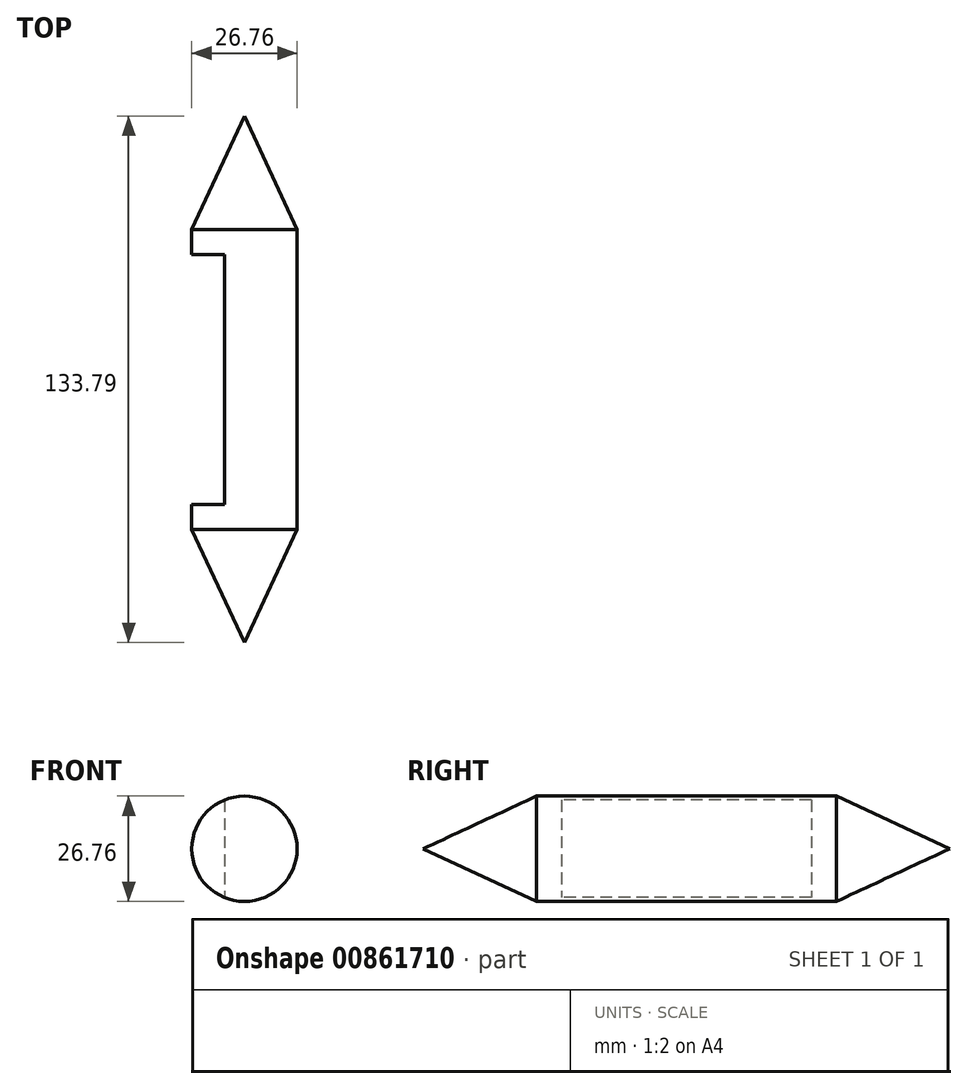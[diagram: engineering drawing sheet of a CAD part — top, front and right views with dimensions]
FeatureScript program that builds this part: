
annotation { "Feature Type Name" : "Feature", "Feature Type Description" : "" }
export const myFeature = defineFeature(function(context is Context, id is Id, definition is map)
    precondition{}
    {
        {
            var Q0;
            Q0=qCreatedBy(makeId("Top.planeOp"),FACE);
            var sketch = newSketch(context, id + "F0", { "sketchPlane" : qUnion([Q0])});
            skLineSegment(sketch, "E0", {"start": v(0, -133.8) * mm, "end": v(-13.38, -105) * mm});
            skLineSegment(sketch, "E1", {"start": v(-13.38, -105) * mm, "end": v(-13.38, -28.8) * mm});
            skLineSegment(sketch, "E2", {"start": v(-13.38, -28.8) * mm, "end": v(0, 0) * mm});
            skLineSegment(sketch, "E3", {"start": v(0, -133.8) * mm, "end": v(0, 0) * mm});
            skSolve(sketch);
        }
        {
            var Q0;
            Q0=makeQuery(id+"F0.imprint","IMPRINT",FACE,{"disambiguationData":[TD([[makeQuery(id+"F0.imprint","IMPRINT",EDGE,{"derivedFrom":sQuery(id+"F0.wireOp",EDGE,"E0")}),-1.0]])]});
            var Q1;
            Q1=sQuery(id+"F0.wireOp",EDGE,"E3");
            revolve(context, id + "F1", {"surfaceOperationType" : NewSurfaceOperationType.NEW, "entities" : qUnion([Q0]), "axis" : qUnion([Q1]), "revolveType" : RevolveType.FULL});
        }
        {
            var Q0;
            Q0=qCreatedBy(makeId("Top.planeOp"),FACE);
            var sketch = newSketch(context, id + "F2", { "sketchPlane" : qUnion([Q0])});
            skLineSegment(sketch, "E4.bottom", {"start": v(-5.08, -35.15) * mm, "end": v(-47.95, -35.15) * mm});
            skLineSegment(sketch, "E4.top", {"start": v(-5.08, -98.65) * mm, "end": v(-47.95, -98.65) * mm});
            skLineSegment(sketch, "E4.left", {"start": v(-5.08, -35.15) * mm, "end": v(-5.08, -98.65) * mm});
            skLineSegment(sketch, "E4.right", {"start": v(-47.95, -35.15) * mm, "end": v(-47.95, -98.65) * mm});
            skPoint(sketch, "E4.middle", {"position": v(-26.52, -66.9) * mm});
            skSolve(sketch);
        }
        {
            var Q0;
            Q0=makeQuery(id+"F2.imprint","IMPRINT",FACE,{"disambiguationData":[TD([[makeQuery(id+"F2.imprint","IMPRINT",EDGE,{"derivedFrom":sQuery(id+"F2.wireOp",EDGE,"E4.bottom")}),1.0]])]});
            extrude(context, id + "F3", {"entities" : qUnion([Q0]), "operationType" : NewBodyOperationType.REMOVE, "endBound" : BoundingType.SYMMETRIC, "depth" : 25.4 * mm, "offsetDistance" : 25.4 * mm});
        }
    });
